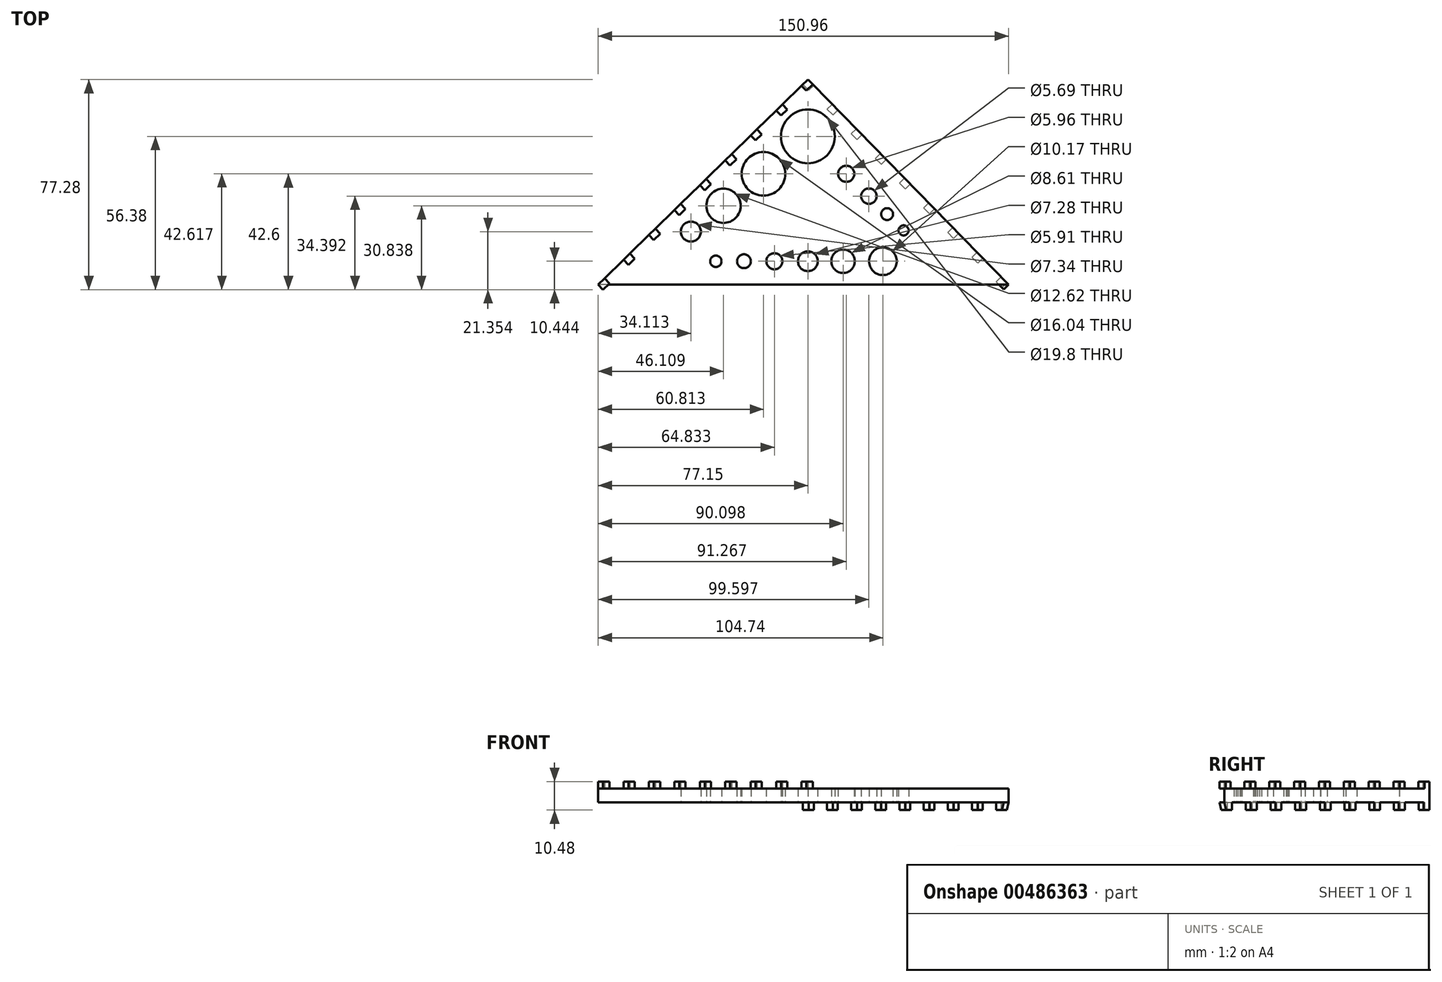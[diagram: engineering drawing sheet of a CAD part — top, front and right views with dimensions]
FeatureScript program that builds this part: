
annotation { "Feature Type Name" : "Feature", "Feature Type Description" : "" }
export const myFeature = defineFeature(function(context is Context, id is Id, definition is map)
    precondition{}
    {
        {
            var Q0;
            Q0=qCreatedBy(makeId("Top.planeOp"),FACE);
            var sketch = newSketch(context, id + "F0", { "sketchPlane" : qUnion([Q0])});
            skLineSegment(sketch, "E0", {"start": v(0, 0) * mm, "end": v(-77.15, 0) * mm});
            skLineSegment(sketch, "E1", {"start": v(-77.15, 0) * mm, "end": v(0, 75.46) * mm});
            skLineSegment(sketch, "E2", {"start": v(0, 75.46) * mm, "end": v(73.8, 0) * mm});
            skLineSegment(sketch, "E3", {"start": v(73.8, 0) * mm, "end": v(0, 0) * mm});
            skCircle(sketch, "E4", {"center": v(0, 54.56) * mm, "radius": 9.9 * mm});
            skCircle(sketch, "E5", {"center": v(-16.34, 40.78) * mm, "radius": 8.02 * mm});
            skCircle(sketch, "E6", {"center": v(-31.04, 29.02) * mm, "radius": 6.3 * mm});
            skCircle(sketch, "E7", {"center": v(-43.04, 19.53) * mm, "radius": 3.67 * mm});
            skCircle(sketch, "E8", {"center": v(-33.85, 8.62) * mm, "radius": 2.1 * mm});
            skCircle(sketch, "E9", {"center": v(-23.51, 8.62) * mm, "radius": 2.55 * mm});
            skCircle(sketch, "E10", {"center": v(-12.32, 8.62) * mm, "radius": 2.95 * mm});
            skCircle(sketch, "E11", {"center": v(0, 8.62) * mm, "radius": 3.64 * mm});
            skCircle(sketch, "E12", {"center": v(12.95, 8.62) * mm, "radius": 4.3 * mm});
            skCircle(sketch, "E13", {"center": v(27.6, 8.62) * mm, "radius": 5.09 * mm});
            skCircle(sketch, "E14", {"center": v(14.12, 40.8) * mm, "radius": 2.98 * mm});
            skCircle(sketch, "E15", {"center": v(22.45, 32.57) * mm, "radius": 2.84 * mm});
            skCircle(sketch, "E16", {"center": v(29.14, 25.97) * mm, "radius": 2.2 * mm});
            skCircle(sketch, "E17", {"center": v(35.2, 19.97) * mm, "radius": 1.87 * mm});
            skSolve(sketch);
        }
        {
            var Q0;
            Q0=makeQuery(id+"F0.imprint","IMPRINT",FACE,{"disambiguationData":[TD([[makeQuery(id+"F0.imprint","IMPRINT",EDGE,{"derivedFrom":sQuery(id+"F0.wireOp",EDGE,"E0")}),-1.0]])]});
            extrude(context, id + "F1", {"entities" : qUnion([Q0]), "depth" : 5.08 * mm});
        }
        {
            var Q0;
            Q0=makeQuery(id+"F1.opExtrude","SWEPT_FACE",FACE,{"disambiguationData":[OSD([sQuery(id+"F0.wireOp",EDGE,"E2")])]});
            var sketch = newSketch(context, id + "F2", { "sketchPlane" : qUnion([Q0])});
            skLineSegment(sketch, "E18", {"start": v(53.94, 0) * mm, "end": v(53.94, -2.89) * mm});
            skLineSegment(sketch, "E19", {"start": v(53.94, -2.89) * mm, "end": v(50.87, -2.89) * mm});
            skLineSegment(sketch, "E20", {"start": v(50.87, -2.89) * mm, "end": v(50.87, 0) * mm});
            skLineSegment(sketch, "E21.1.0.0", {"start": v(41.24, 0) * mm, "end": v(41.24, -2.89) * mm});
            skLineSegment(sketch, "E21.1.0.1", {"start": v(41.24, -2.89) * mm, "end": v(38.17, -2.89) * mm});
            skLineSegment(sketch, "E21.2.0.0", {"start": v(28.54, 0) * mm, "end": v(28.54, -2.89) * mm});
            skLineSegment(sketch, "E21.2.0.1", {"start": v(28.54, -2.89) * mm, "end": v(25.47, -2.89) * mm});
            skLineSegment(sketch, "E21.3.0.0", {"start": v(15.84, 0) * mm, "end": v(15.84, -2.89) * mm});
            skLineSegment(sketch, "E21.3.0.1", {"start": v(15.84, -2.89) * mm, "end": v(12.77, -2.89) * mm});
            skLineSegment(sketch, "E21.4.0.0", {"start": v(3.14, 0) * mm, "end": v(3.14, -2.89) * mm});
            skLineSegment(sketch, "E21.4.0.1", {"start": v(3.14, -2.89) * mm, "end": v(0.07, -2.89) * mm});
            skLineSegment(sketch, "E21.5.0.0", {"start": v(-9.56, 0) * mm, "end": v(-9.56, -2.89) * mm});
            skLineSegment(sketch, "E21.5.0.1", {"start": v(-9.56, -2.89) * mm, "end": v(-12.63, -2.89) * mm});
            skLineSegment(sketch, "E21.6.0.0", {"start": v(-22.26, 0) * mm, "end": v(-22.26, -2.89) * mm});
            skLineSegment(sketch, "E21.6.0.1", {"start": v(-22.26, -2.89) * mm, "end": v(-25.33, -2.89) * mm});
            skLineSegment(sketch, "E21.7.0.0", {"start": v(-34.96, 0) * mm, "end": v(-34.96, -2.89) * mm});
            skLineSegment(sketch, "E21.7.0.1", {"start": v(-34.96, -2.89) * mm, "end": v(-38.03, -2.89) * mm});
            skLineSegment(sketch, "E21.8.0.0", {"start": v(-47.66, 0) * mm, "end": v(-47.66, -2.89) * mm});
            skLineSegment(sketch, "E21.8.0.1", {"start": v(-47.66, -2.89) * mm, "end": v(-50.73, -2.89) * mm});
            skLineSegment(sketch, "E21.direction1", {"start": v(50.87, -2.89) * mm, "end": v(38.17, -2.89) * mm, "construction": true});
            skLineSegment(sketch, "E22", {"start": v(-50.73, -2.89) * mm, "end": v(-51.61, 0) * mm});
            skLineSegment(sketch, "E23", {"start": v(-38.03, -2.89) * mm, "end": v(-38.03, 0) * mm});
            skLineSegment(sketch, "E24", {"start": v(-25.33, -2.89) * mm, "end": v(-25.33, 0) * mm});
            skLineSegment(sketch, "E25", {"start": v(-12.63, -2.89) * mm, "end": v(-12.63, 0) * mm});
            skLineSegment(sketch, "E26", {"start": v(0.07, -2.89) * mm, "end": v(0.07, 0) * mm});
            skLineSegment(sketch, "E27", {"start": v(12.77, -2.89) * mm, "end": v(12.77, 0) * mm});
            skLineSegment(sketch, "E28", {"start": v(25.47, -2.89) * mm, "end": v(25.47, 0) * mm});
            skLineSegment(sketch, "E29", {"start": v(38.17, -2.89) * mm, "end": v(38.17, 0) * mm});
            skLineSegment(sketch, "E30", {"start": v(53.94, 0) * mm, "end": v(-51.61, 0) * mm});
            skSolve(sketch);
        }
        {
            var Q0;
            Q0 = qSketchRegion(id + "F2", true);
            extrude(context, id + "F3", {"entities" : qUnion([Q0]), "operationType" : NewBodyOperationType.ADD, "oppositeDirection" : true, "depth" : 2.54 * mm});
        }
        {
            var Q0;
            Q0=makeQuery(id+"F3.boolean.opBoolean","MERGE",FACE,{"derivedFrom":[makeQuery(id+"F1.opExtrude","SWEPT_FACE",FACE,{"disambiguationData":[OSD([sQuery(id+"F0.wireOp",EDGE,"E1")])]}),makeQuery(id+"F3.opExtrude","SWEPT_FACE",FACE,{"disambiguationData":[OSD([sQuery(id+"F2.wireOp",EDGE,"E18")])]})]});
            var sketch = newSketch(context, id + "F4", { "sketchPlane" : qUnion([Q0])});
            skLineSegment(sketch, "E31", {"start": v(55.15, 5.08) * mm, "end": v(55.15, 7.6) * mm});
            skLineSegment(sketch, "E32", {"start": v(55.15, 7.6) * mm, "end": v(51.9, 7.6) * mm});
            skLineSegment(sketch, "E33", {"start": v(51.9, 7.6) * mm, "end": v(51.9, 5.08) * mm});
            skLineSegment(sketch, "E34.1.0.0", {"start": v(38.81, 7.6) * mm, "end": v(38.81, 5.08) * mm});
            skLineSegment(sketch, "E34.1.0.1", {"start": v(42.07, 7.6) * mm, "end": v(38.81, 7.6) * mm});
            skLineSegment(sketch, "E34.1.0.2", {"start": v(42.07, 5.08) * mm, "end": v(42.07, 7.6) * mm});
            skLineSegment(sketch, "E34.2.0.0", {"start": v(25.73, 7.6) * mm, "end": v(25.73, 5.08) * mm});
            skLineSegment(sketch, "E34.2.0.1", {"start": v(28.99, 7.6) * mm, "end": v(25.73, 7.6) * mm});
            skLineSegment(sketch, "E34.2.0.2", {"start": v(28.99, 5.08) * mm, "end": v(28.99, 7.6) * mm});
            skLineSegment(sketch, "E34.3.0.0", {"start": v(12.65, 7.6) * mm, "end": v(12.65, 5.08) * mm});
            skLineSegment(sketch, "E34.3.0.1", {"start": v(15.9, 7.6) * mm, "end": v(12.65, 7.6) * mm});
            skLineSegment(sketch, "E34.3.0.2", {"start": v(15.9, 5.08) * mm, "end": v(15.9, 7.6) * mm});
            skLineSegment(sketch, "E34.4.0.0", {"start": v(-0.43, 7.6) * mm, "end": v(-0.43, 5.08) * mm});
            skLineSegment(sketch, "E34.4.0.1", {"start": v(2.83, 7.6) * mm, "end": v(-0.43, 7.6) * mm});
            skLineSegment(sketch, "E34.4.0.2", {"start": v(2.83, 5.08) * mm, "end": v(2.83, 7.6) * mm});
            skLineSegment(sketch, "E34.5.0.0", {"start": v(-13.51, 7.6) * mm, "end": v(-13.51, 5.08) * mm});
            skLineSegment(sketch, "E34.5.0.1", {"start": v(-10.26, 7.6) * mm, "end": v(-13.51, 7.6) * mm});
            skLineSegment(sketch, "E34.5.0.2", {"start": v(-10.26, 5.08) * mm, "end": v(-10.26, 7.6) * mm});
            skLineSegment(sketch, "E34.6.0.0", {"start": v(-26.6, 7.6) * mm, "end": v(-26.6, 5.08) * mm});
            skLineSegment(sketch, "E34.6.0.1", {"start": v(-23.34, 7.6) * mm, "end": v(-26.6, 7.6) * mm});
            skLineSegment(sketch, "E34.6.0.2", {"start": v(-23.34, 5.08) * mm, "end": v(-23.34, 7.6) * mm});
            skLineSegment(sketch, "E34.7.0.0", {"start": v(-39.68, 7.6) * mm, "end": v(-39.68, 5.08) * mm});
            skLineSegment(sketch, "E34.7.0.1", {"start": v(-36.42, 7.6) * mm, "end": v(-39.68, 7.6) * mm});
            skLineSegment(sketch, "E34.7.0.2", {"start": v(-36.42, 5.08) * mm, "end": v(-36.42, 7.6) * mm});
            skLineSegment(sketch, "E34.8.0.0", {"start": v(-52.76, 7.6) * mm, "end": v(-52.76, 5.08) * mm});
            skLineSegment(sketch, "E34.8.0.1", {"start": v(-49.5, 7.6) * mm, "end": v(-52.76, 7.6) * mm});
            skLineSegment(sketch, "E34.8.0.2", {"start": v(-49.5, 5.08) * mm, "end": v(-49.5, 7.6) * mm});
            skLineSegment(sketch, "E34.direction1", {"start": v(51.9, 5.08) * mm, "end": v(38.81, 5.08) * mm, "construction": true});
            skSolve(sketch);
        }
        {
            var Q0;
            {var subQ0=sQuery(id+"F4.wireOp",EDGE,"E34.8.0.0");Q0=makeQuery(id+"F4.imprint","IMPRINT",FACE,{"disambiguationData":[TD([[makeQuery(id+"F4.imprint","IMPRINT",EDGE,{"derivedFrom":subQ0}),1.0]])]});}
            var Q1;
            {var subQ0=sQuery(id+"F4.wireOp",EDGE,"E34.7.0.0");Q1=makeQuery(id+"F4.imprint","IMPRINT",FACE,{"disambiguationData":[TD([[makeQuery(id+"F4.imprint","IMPRINT",EDGE,{"derivedFrom":subQ0}),1.0]])]});}
            var Q2;
            {var subQ0=sQuery(id+"F4.wireOp",EDGE,"E34.6.0.0");Q2=makeQuery(id+"F4.imprint","IMPRINT",FACE,{"disambiguationData":[TD([[makeQuery(id+"F4.imprint","IMPRINT",EDGE,{"derivedFrom":subQ0}),1.0]])]});}
            var Q3;
            {var subQ0=sQuery(id+"F4.wireOp",EDGE,"E34.5.0.0");Q3=makeQuery(id+"F4.imprint","IMPRINT",FACE,{"disambiguationData":[TD([[makeQuery(id+"F4.imprint","IMPRINT",EDGE,{"derivedFrom":subQ0}),1.0]])]});}
            var Q4;
            {var subQ0=sQuery(id+"F4.wireOp",EDGE,"E34.4.0.0");Q4=makeQuery(id+"F4.imprint","IMPRINT",FACE,{"disambiguationData":[TD([[makeQuery(id+"F4.imprint","IMPRINT",EDGE,{"derivedFrom":subQ0}),1.0]])]});}
            var Q5;
            {var subQ0=sQuery(id+"F4.wireOp",EDGE,"E34.3.0.0");Q5=makeQuery(id+"F4.imprint","IMPRINT",FACE,{"disambiguationData":[TD([[makeQuery(id+"F4.imprint","IMPRINT",EDGE,{"derivedFrom":subQ0}),1.0]])]});}
            var Q6;
            {var subQ0=sQuery(id+"F4.wireOp",EDGE,"E34.2.0.0");Q6=makeQuery(id+"F4.imprint","IMPRINT",FACE,{"disambiguationData":[TD([[makeQuery(id+"F4.imprint","IMPRINT",EDGE,{"derivedFrom":subQ0}),1.0]])]});}
            var Q7;
            {var subQ0=sQuery(id+"F4.wireOp",EDGE,"E34.1.0.0");Q7=makeQuery(id+"F4.imprint","IMPRINT",FACE,{"disambiguationData":[TD([[makeQuery(id+"F4.imprint","IMPRINT",EDGE,{"derivedFrom":subQ0}),1.0]])]});}
            var Q8;
            {var subQ0=sQuery(id+"F4.wireOp",EDGE,"E31");Q8=makeQuery(id+"F4.imprint","IMPRINT",FACE,{"disambiguationData":[TD([[makeQuery(id+"F4.imprint","IMPRINT",EDGE,{"derivedFrom":subQ0}),1.0]])]});}
            extrude(context, id + "F5", {"entities" : qUnion([Q0, Q1, Q2, Q3, Q4, Q5, Q6, Q7, Q8]), "operationType" : NewBodyOperationType.ADD, "oppositeDirection" : true, "depth" : 2.54 * mm});
        }
    });
